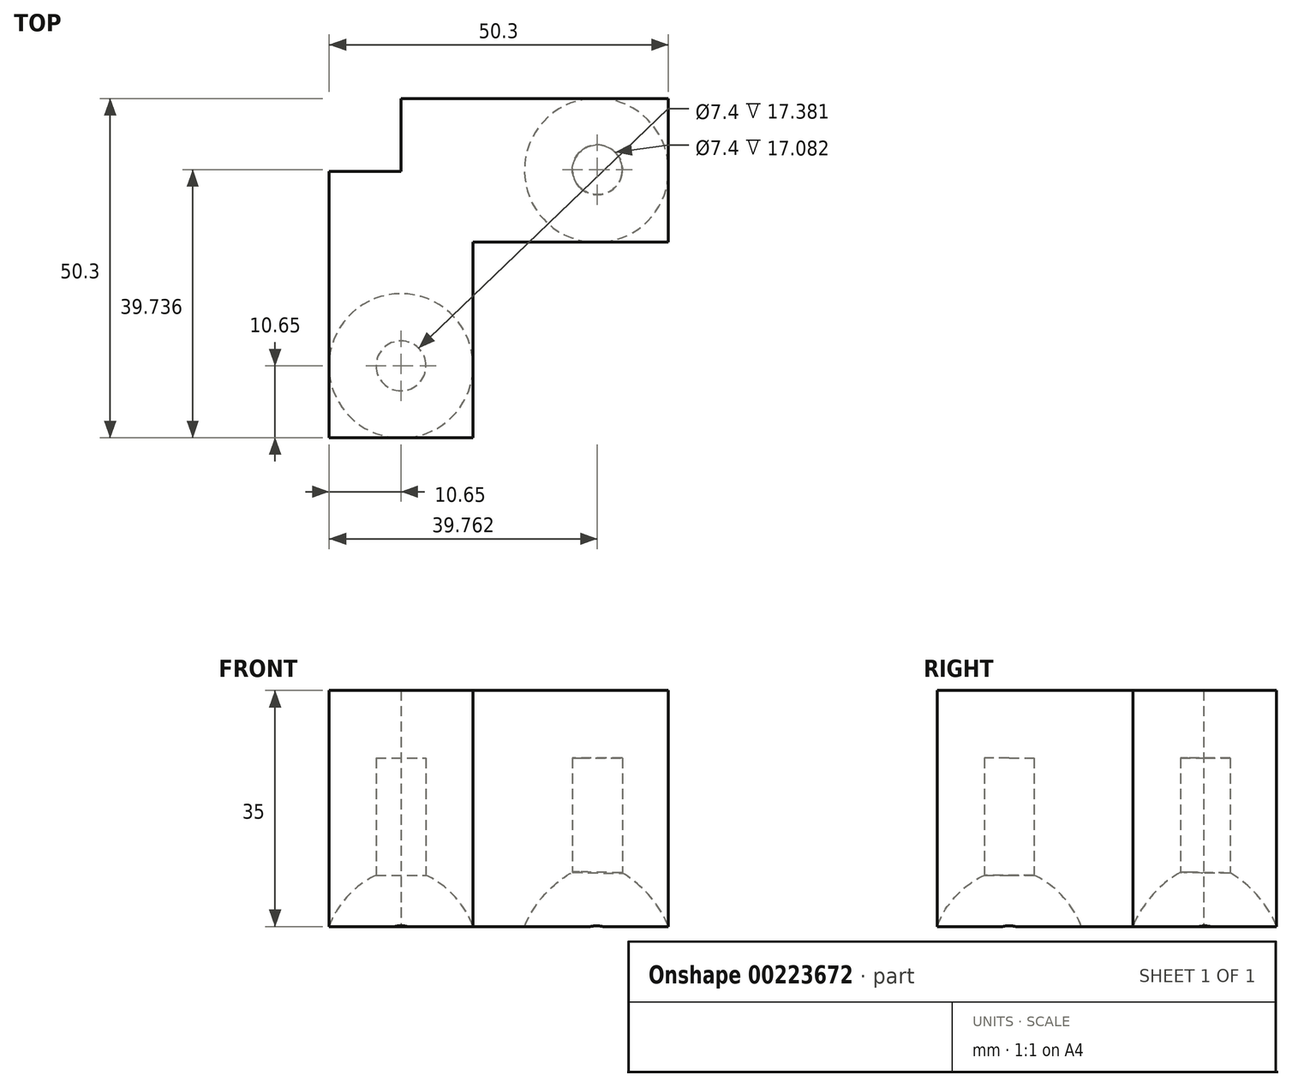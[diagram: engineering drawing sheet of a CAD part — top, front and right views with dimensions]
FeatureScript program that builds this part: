
annotation { "Feature Type Name" : "Feature", "Feature Type Description" : "" }
export const myFeature = defineFeature(function(context is Context, id is Id, definition is map)
    precondition{}
    {
        {
            var Q0;
            Q0=qCreatedBy(makeId("Top.planeOp"),FACE);
            var sketch = newSketch(context, id + "F0", { "sketchPlane" : qUnion([Q0])});
            skLineSegment(sketch, "E0.bottom", {"start": v(-10.65, 21.3) * mm, "end": v(39.65, 21.3) * mm});
            skLineSegment(sketch, "E0.top", {"start": v(-10.65, 0) * mm, "end": v(39.65, 0) * mm});
            skLineSegment(sketch, "E0.left", {"start": v(-10.65, 21.3) * mm, "end": v(-10.65, 0) * mm});
            skLineSegment(sketch, "E0.right", {"start": v(39.65, 21.3) * mm, "end": v(39.65, 0) * mm});
            skLineSegment(sketch, "E1.bottom", {"start": v(-10.65, 21.3) * mm, "end": v(10.65, 21.3) * mm});
            skLineSegment(sketch, "E1.top", {"start": v(-10.65, -29) * mm, "end": v(10.65, -29) * mm});
            skLineSegment(sketch, "E1.left", {"start": v(-10.65, 21.3) * mm, "end": v(-10.65, -29) * mm});
            skLineSegment(sketch, "E1.right", {"start": v(10.65, 21.3) * mm, "end": v(10.65, -29) * mm});
            skPoint(sketch, "E2", {"position": v(0, 21.3) * mm});
            skPoint(sketch, "E3", {"position": v(0, 0) * mm});
            skCircle(sketch, "E4", {"center": v(29, 10.65) * mm, "radius": 10.65 * mm});
            skCircle(sketch, "E5", {"center": v(0, -18.35) * mm, "radius": 10.65 * mm});
            skLineSegment(sketch, "E6", {"start": v(18.35, 10.52) * mm, "end": v(-10.65, 10.52) * mm});
            skLineSegment(sketch, "E7", {"start": v(0, 21.3) * mm, "end": v(0, -7.7) * mm});
            skLineSegment(sketch, "E8", {"start": v(29, 10.65) * mm, "end": v(29, 0) * mm});
            skSolve(sketch);
        }
        {
            var Q0;
            {var subQ0=sQuery(id+"F0.wireOp",EDGE,"E1.left");var subQ1=sQuery(id+"F0.wireOp",EDGE,"E1.bottom");var subQ2=makeQuery(id+"F0.imprint","INTERSECT",VERTEX,{"derivedFrom":[subQ1,subQ0]});Q0=makeQuery(id+"F0.imprint","IMPRINT",FACE,{"disambiguationData":[TD([[makeQuery(id+"F0.imprint","IMPRINT",EDGE,{"disambiguationData":[TD([[subQ2,-1.0]])],"derivedFrom":subQ1}),-1.0]])]});}
            var Q1;
            {var subQ0=sQuery(id+"F0.wireOp",EDGE,"E1.right");var subQ5=sQuery(id+"F0.wireOp",EDGE,"E6");var subQ6=makeQuery(id+"F0.imprint","INTERSECT",VERTEX,{"derivedFrom":[subQ0,subQ5]});Q1=makeQuery(id+"F0.imprint","IMPRINT",FACE,{"disambiguationData":[TD([[makeQuery(id+"F0.imprint","IMPRINT",EDGE,{"disambiguationData":[TD([[subQ6,-1.0]])],"derivedFrom":subQ5}),-1.0]])]});}
            var Q2;
            {var subQ3=sQuery(id+"F0.wireOp",EDGE,"E4");var subQ5=sQuery(id+"F0.wireOp",EDGE,"E6");var subQ7=makeQuery(id+"F0.imprint","INTERSECT",VERTEX,{"derivedFrom":[subQ3,subQ5]});Q2=makeQuery(id+"F0.imprint","IMPRINT",FACE,{"disambiguationData":[TD([[makeQuery(id+"F0.imprint","IMPRINT",EDGE,{"disambiguationData":[TD([[subQ7,1.0]])],"derivedFrom":subQ3}),-1.0]])]});}
            var Q3;
            {var subQ0=sQuery(id+"F0.wireOp",EDGE,"E0.right");var subQ1=sQuery(id+"F0.wireOp",EDGE,"E0.bottom");var subQ2=makeQuery(id+"F0.imprint","INTERSECT",VERTEX,{"derivedFrom":[subQ1,subQ0]});Q3=makeQuery(id+"F0.imprint","IMPRINT",FACE,{"disambiguationData":[TD([[makeQuery(id+"F0.imprint","IMPRINT",EDGE,{"disambiguationData":[TD([[subQ2,1.0]])],"derivedFrom":subQ1}),-1.0]])]});}
            var Q4;
            {var subQ0=sQuery(id+"F0.wireOp",EDGE,"E0.right");var subQ1=sQuery(id+"F0.wireOp",EDGE,"E0.top");var subQ2=makeQuery(id+"F0.imprint","INTERSECT",VERTEX,{"derivedFrom":[subQ1,subQ0]});Q4=makeQuery(id+"F0.imprint","IMPRINT",FACE,{"disambiguationData":[TD([[makeQuery(id+"F0.imprint","IMPRINT",EDGE,{"disambiguationData":[TD([[subQ2,1.0]])],"derivedFrom":subQ1}),1.0]])]});}
            var Q5;
            {var subQ0=sQuery(id+"F0.wireOp",EDGE,"E1.right");var subQ1=sQuery(id+"F0.wireOp",EDGE,"E0.top");var subQ2=makeQuery(id+"F0.imprint","INTERSECT",VERTEX,{"derivedFrom":[subQ1,subQ0]});Q5=makeQuery(id+"F0.imprint","IMPRINT",FACE,{"disambiguationData":[TD([[makeQuery(id+"F0.imprint","IMPRINT",EDGE,{"disambiguationData":[TD([[subQ2,-1.0]])],"derivedFrom":subQ1}),1.0]])]});}
            var Q6;
            {var subQ0=sQuery(id+"F0.wireOp",EDGE,"E1.right");var subQ1=sQuery(id+"F0.wireOp",EDGE,"E0.top");var subQ2=makeQuery(id+"F0.imprint","INTERSECT",VERTEX,{"derivedFrom":[subQ1,subQ0]});Q6=makeQuery(id+"F0.imprint","IMPRINT",FACE,{"disambiguationData":[TD([[makeQuery(id+"F0.imprint","IMPRINT",EDGE,{"disambiguationData":[TD([[subQ2,1.0]])],"derivedFrom":subQ1}),1.0]])]});}
            var Q7;
            {var subQ0=sQuery(id+"F0.wireOp",EDGE,"E1.left");var subQ1=sQuery(id+"F0.wireOp",EDGE,"E0.top");var subQ2=makeQuery(id+"F0.imprint","INTERSECT",VERTEX,{"derivedFrom":[subQ1,subQ0]});Q7=makeQuery(id+"F0.imprint","IMPRINT",FACE,{"disambiguationData":[TD([[makeQuery(id+"F0.imprint","IMPRINT",EDGE,{"disambiguationData":[TD([[subQ2,-1.0]])],"derivedFrom":subQ1}),1.0]])]});}
            var Q8;
            {var subQ0=sQuery(id+"F0.wireOp",EDGE,"E1.left");var subQ1=sQuery(id+"F0.wireOp",EDGE,"E0.top");var subQ2=makeQuery(id+"F0.imprint","INTERSECT",VERTEX,{"derivedFrom":[subQ1,subQ0]});Q8=makeQuery(id+"F0.imprint","IMPRINT",FACE,{"disambiguationData":[TD([[makeQuery(id+"F0.imprint","IMPRINT",EDGE,{"disambiguationData":[TD([[subQ2,-1.0]])],"derivedFrom":subQ1}),-1.0]])]});}
            var Q9;
            {var subQ0=sQuery(id+"F0.wireOp",EDGE,"E1.right");var subQ1=sQuery(id+"F0.wireOp",EDGE,"E0.top");var subQ2=makeQuery(id+"F0.imprint","INTERSECT",VERTEX,{"derivedFrom":[subQ1,subQ0]});Q9=makeQuery(id+"F0.imprint","IMPRINT",FACE,{"disambiguationData":[TD([[makeQuery(id+"F0.imprint","IMPRINT",EDGE,{"disambiguationData":[TD([[subQ2,1.0]])],"derivedFrom":subQ1}),-1.0]])]});}
            var Q10;
            {var subQ0=sQuery(id+"F0.wireOp",EDGE,"E1.left");var subQ1=sQuery(id+"F0.wireOp",EDGE,"E1.top");var subQ2=makeQuery(id+"F0.imprint","INTERSECT",VERTEX,{"derivedFrom":[subQ1,subQ0]});Q10=makeQuery(id+"F0.imprint","IMPRINT",FACE,{"disambiguationData":[TD([[makeQuery(id+"F0.imprint","IMPRINT",EDGE,{"disambiguationData":[TD([[subQ2,-1.0]])],"derivedFrom":subQ1}),1.0]])]});}
            var Q11;
            {var subQ0=sQuery(id+"F0.wireOp",EDGE,"E1.right");var subQ1=sQuery(id+"F0.wireOp",EDGE,"E1.top");var subQ2=makeQuery(id+"F0.imprint","INTERSECT",VERTEX,{"derivedFrom":[subQ1,subQ0]});Q11=makeQuery(id+"F0.imprint","IMPRINT",FACE,{"disambiguationData":[TD([[makeQuery(id+"F0.imprint","IMPRINT",EDGE,{"disambiguationData":[TD([[subQ2,1.0]])],"derivedFrom":subQ1}),1.0]])]});}
            var Q12;
            {var subQ0=sQuery(id+"F0.wireOp",EDGE,"E5");var subQ1=makeQuery(id+"F0.imprint","INTERSECT",VERTEX,{"derivedFrom":[subQ0,sQuery(id+"F0.wireOp",EDGE,"E7")]});Q12=makeQuery(id+"F0.imprint","IMPRINT",FACE,{"disambiguationData":[TD([[makeQuery(id+"F0.imprint","IMPRINT",EDGE,{"disambiguationData":[TD([[subQ1,1.0]])],"derivedFrom":subQ0}),1.0]])]});}
            var Q13;
            {var subQ0=sQuery(id+"F0.wireOp",EDGE,"E4");var subQ1=makeQuery(id+"F0.imprint","INTERSECT",VERTEX,{"derivedFrom":[sQuery(id+"F0.wireOp",EDGE,"E0.bottom"),subQ0]});Q13=makeQuery(id+"F0.imprint","IMPRINT",FACE,{"disambiguationData":[TD([[makeQuery(id+"F0.imprint","IMPRINT",EDGE,{"disambiguationData":[TD([[subQ1,1.0]])],"derivedFrom":subQ0}),1.0]])]});}
            extrude(context, id + "F1", {"entities" : qUnion([Q0, Q1, Q2, Q3, Q4, Q5, Q6, Q7, Q8, Q9, Q10, Q11, Q12, Q13]), "depth" : 35 * mm});
        }
        {
            var Q0;
            Q0=qCreatedBy(makeId("Right.planeOp"),FACE);
            var sketch = newSketch(context, id + "F2", { "sketchPlane" : qUnion([Q0])});
            skArc(sketch, "E9", {"start": v(-18.35, 8.8) * mm, "mid": v(-24.87, 5.82) * mm, "end": v(-29.04, 0) * mm});
            skLineSegment(sketch, "E10", {"start": v(-18.35, 0) * mm, "end": v(-18.35, 12.48) * mm, "construction": true});
            skLineSegment(sketch, "E11", {"start": v(-29.04, 0) * mm, "end": v(-18.35, 0) * mm});
            skLineSegment(sketch, "E12", {"start": v(-18.35, 0) * mm, "end": v(-18.35, 8.8) * mm});
            skSolve(sketch);
        }
        {
            var Q0;
            Q0 = qSketchRegion(id + "F2", true);
            var Q1;
            Q1=sQuery(id+"F2.wireOp",EDGE,"E10");
            revolve(context, id + "F3", {"operationType" : NewBodyOperationType.REMOVE, "entities" : qUnion([Q0]), "axis" : qUnion([Q1]), "revolveType" : RevolveType.FULL, "oppositeDirection" : true});
        }
        {
            var Q0;
            Q0=qCreatedBy(makeId("Front.planeOp"),FACE);
            cPlane(context, id + "F4", {"entities" : qUnion([Q0]), "cplaneType" : CPlaneType.OFFSET, "offset" : 10.65 * mm, "oppositeDirection" : true, "width" : 150 * mm, "height" : 150 * mm});
        }
        {
            var Q0;
            Q0=qCreatedBy(makeId("Top.planeOp"),FACE);
            var sketch = newSketch(context, id + "F5", { "sketchPlane" : qUnion([Q0])});
            skCircle(sketch, "E13", {"center": v(0, -18.35) * mm, "radius": 3.7 * mm});
            skSolve(sketch);
        }
        {
            var Q0;
            Q0 = qSketchRegion(id + "F5", true);
            extrude(context, id + "F6", {"entities" : qUnion([Q0]), "operationType" : NewBodyOperationType.REMOVE, "depth" : 25 * mm});
        }
        {
            var Q0;
            Q0=qCreatedBy(makeId("Top.planeOp"),FACE);
            var sketch = newSketch(context, id + "F7", { "sketchPlane" : qUnion([Q0])});
            skCircle(sketch, "E14", {"center": v(29.11, 10.74) * mm, "radius": 3.7 * mm});
            skSolve(sketch);
        }
        {
            var Q0;
            Q0=makeQuery(id+"F7.imprint","IMPRINT",FACE,{"disambiguationData":[TD([[makeQuery(id+"F7.imprint","IMPRINT",EDGE,{"derivedFrom":sQuery(id+"F7.wireOp",EDGE,"E14")}),1.0]])]});
            extrude(context, id + "F8", {"entities" : qUnion([Q0]), "operationType" : NewBodyOperationType.REMOVE, "depth" : 25 * mm});
        }
        {
            var Q0;
            Q0=qCreatedBy(id+"F4.planeOp",FACE);
            var sketch = newSketch(context, id + "F9", { "sketchPlane" : qUnion([Q0])});
            skLineSegment(sketch, "E15", {"start": v(29, 0) * mm, "end": v(29, 9.6) * mm});
            skArc(sketch, "E16", {"start": v(29, 9.6) * mm, "mid": v(22.57, 6) * mm, "end": v(18.3, 0) * mm});
            skLineSegment(sketch, "E17", {"start": v(18.3, 0) * mm, "end": v(29, 0) * mm});
            skLineSegment(sketch, "E18", {"start": v(29, 0) * mm, "end": v(29, 23.41) * mm, "construction": true});
            skSolve(sketch);
        }
        {
            var Q0;
            Q0 = qSketchRegion(id + "F9", true);
            var Q1;
            Q1=sQuery(id+"F9.wireOp",EDGE,"E18");
            revolve(context, id + "F10", {"operationType" : NewBodyOperationType.REMOVE, "entities" : qUnion([Q0]), "axis" : qUnion([Q1]), "revolveType" : RevolveType.FULL});
        }
    });
